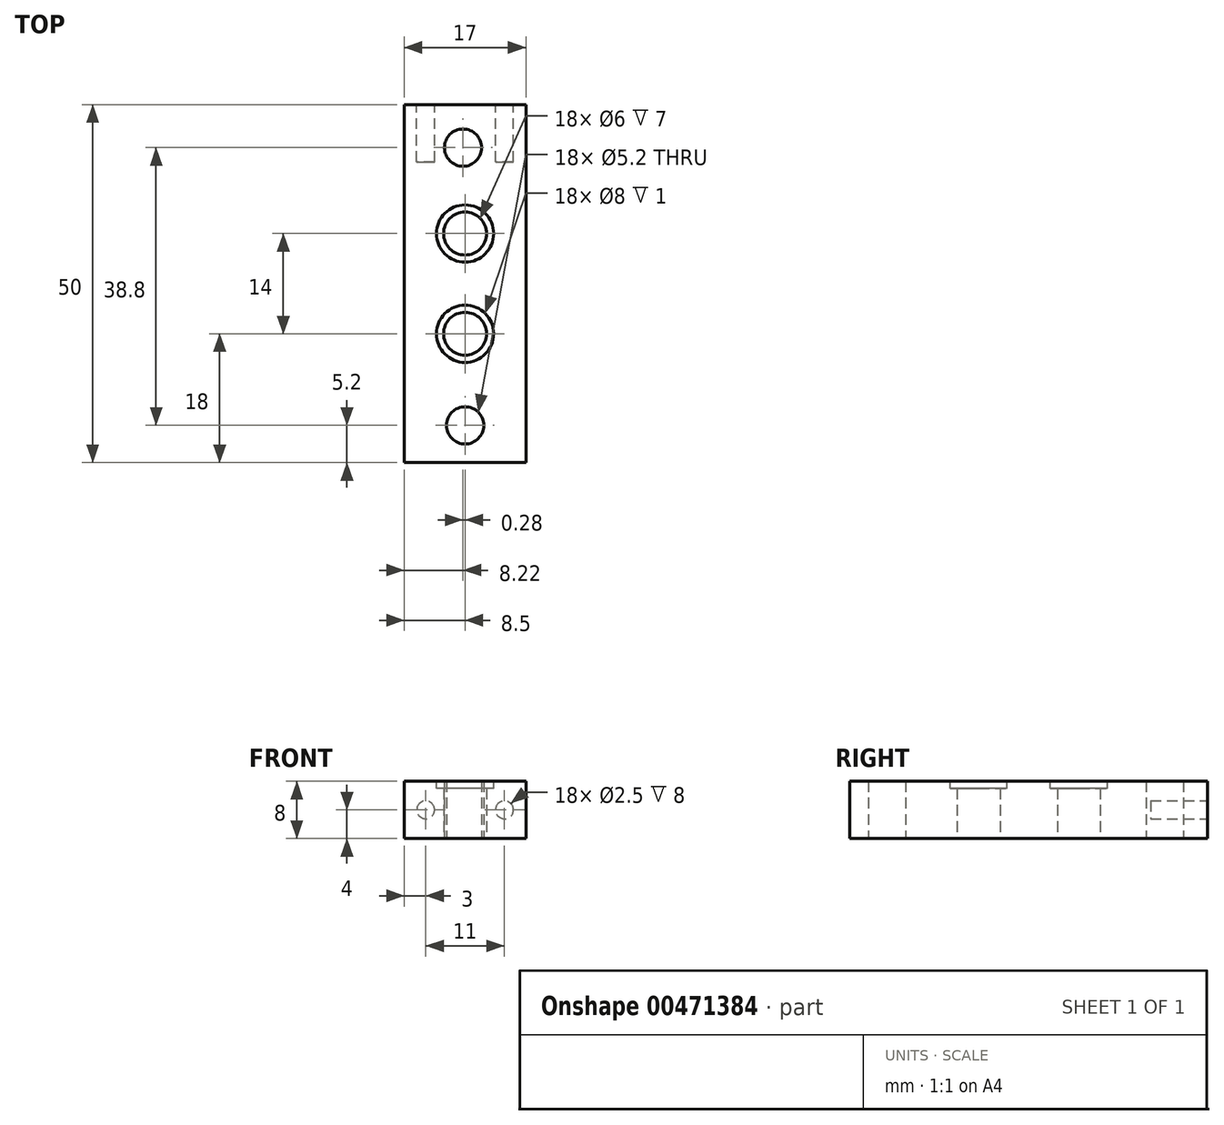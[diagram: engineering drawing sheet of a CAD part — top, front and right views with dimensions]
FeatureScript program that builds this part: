
annotation { "Feature Type Name" : "Feature", "Feature Type Description" : "" }
export const myFeature = defineFeature(function(context is Context, id is Id, definition is map)
    precondition{}
    {
        {
            var Q0;
            Q0=qCreatedBy(makeId("Top.planeOp"),FACE);
            var sketch = newSketch(context, id + "F0", { "sketchPlane" : qUnion([Q0])});
            skLineSegment(sketch, "E0.bottom", {"start": v(0, 0) * mm, "end": v(17, 0) * mm});
            skLineSegment(sketch, "E0.top", {"start": v(0, 50) * mm, "end": v(17, 50) * mm});
            skLineSegment(sketch, "E0.left", {"start": v(0, 0) * mm, "end": v(0, 50) * mm});
            skLineSegment(sketch, "E0.right", {"start": v(17, 0) * mm, "end": v(17, 50) * mm});
            skCircle(sketch, "E1", {"center": v(8.5, 5.2) * mm, "radius": 2.6 * mm});
            skPoint(sketch, "E1.centerSnap0", {"position": v(8.5, 0) * mm});
            skCircle(sketch, "E2", {"center": v(8.5, 18) * mm, "radius": 3 * mm});
            skCircle(sketch, "E3", {"center": v(8.5, 32) * mm, "radius": 3 * mm});
            skCircle(sketch, "E4", {"center": v(8.22, 44) * mm, "radius": 2.6 * mm});
            skSolve(sketch);
        }
        {
            var Q0;
            Q0=makeQuery(id+"F0.imprint","IMPRINT",FACE,{"disambiguationData":[TD([[makeQuery(id+"F0.imprint","IMPRINT",EDGE,{"derivedFrom":sQuery(id+"F0.wireOp",EDGE,"E0.bottom")}),1.0]])]});
            extrude(context, id + "F1", {"entities" : qUnion([Q0]), "depth" : 8 * mm});
        }
        {
            var Q0;
            Q0=makeQuery(id+"F1.opExtrude","CAP_FACE",FACE,{"disambiguationData":[OSD([sQuery(id+"F0.wireOp",EDGE,"E0.bottom"),sQuery(id+"F0.wireOp",EDGE,"E0.top"),sQuery(id+"F0.wireOp",EDGE,"E0.left"),sQuery(id+"F0.wireOp",EDGE,"E0.right"),sQuery(id+"F0.wireOp",EDGE,"E1"),sQuery(id+"F0.wireOp",EDGE,"E2"),sQuery(id+"F0.wireOp",EDGE,"E3"),sQuery(id+"F0.wireOp",EDGE,"E4")])],"isStart":false});
            var sketch = newSketch(context, id + "F2", { "sketchPlane" : qUnion([Q0])});
            skCircle(sketch, "E5", {"center": v(8.5, 32) * mm, "radius": 4 * mm});
            skCircle(sketch, "E6", {"center": v(8.5, 18) * mm, "radius": 4 * mm});
            skSolve(sketch);
        }
        {
            var Q0;
            Q0=makeQuery(id+"F2.imprint","IMPRINT",FACE,{"disambiguationData":[TD([[makeQuery(id+"F2.imprint","IMPRINT",EDGE,{"derivedFrom":sQuery(id+"F2.wireOp",EDGE,"E5")}),1.0]])]});
            var Q1;
            Q1=makeQuery(id+"F2.imprint","IMPRINT",FACE,{"disambiguationData":[TD([[makeQuery(id+"F2.imprint","IMPRINT",EDGE,{"derivedFrom":sQuery(id+"F2.wireOp",EDGE,"E6")}),1.0]])]});
            extrude(context, id + "F3", {"entities" : qUnion([Q0, Q1]), "operationType" : NewBodyOperationType.REMOVE, "oppositeDirection" : true, "depth" : 1 * mm});
        }
        {
            var Q0;
            Q0=makeQuery(id+"F1.opExtrude","SWEPT_FACE",FACE,{"disambiguationData":[OSD([sQuery(id+"F0.wireOp",EDGE,"E0.top")])]});
            var sketch = newSketch(context, id + "F4", { "sketchPlane" : qUnion([Q0])});
            skCircle(sketch, "E7", {"center": v(-14, 4) * mm, "radius": 1.25 * mm});
            skPoint(sketch, "E7.centerSnap0", {"position": v(-17, 4) * mm});
            skPoint(sketch, "E7.perimeterSnap0", {"position": v(-17, 4) * mm});
            skCircle(sketch, "E8", {"center": v(-3, 4) * mm, "radius": 1.25 * mm});
            skSolve(sketch);
        }
        {
            var Q0;
            Q0=makeQuery(id+"F4.imprint","IMPRINT",FACE,{"disambiguationData":[TD([[makeQuery(id+"F4.imprint","IMPRINT",EDGE,{"derivedFrom":sQuery(id+"F4.wireOp",EDGE,"E7")}),1.0]])]});
            var Q1;
            Q1=makeQuery(id+"F4.imprint","IMPRINT",FACE,{"disambiguationData":[TD([[makeQuery(id+"F4.imprint","IMPRINT",EDGE,{"derivedFrom":sQuery(id+"F4.wireOp",EDGE,"E8")}),1.0]])]});
            extrude(context, id + "F5", {"entities" : qUnion([Q0, Q1]), "operationType" : NewBodyOperationType.REMOVE, "oppositeDirection" : true, "depth" : 8 * mm});
        }
    });
